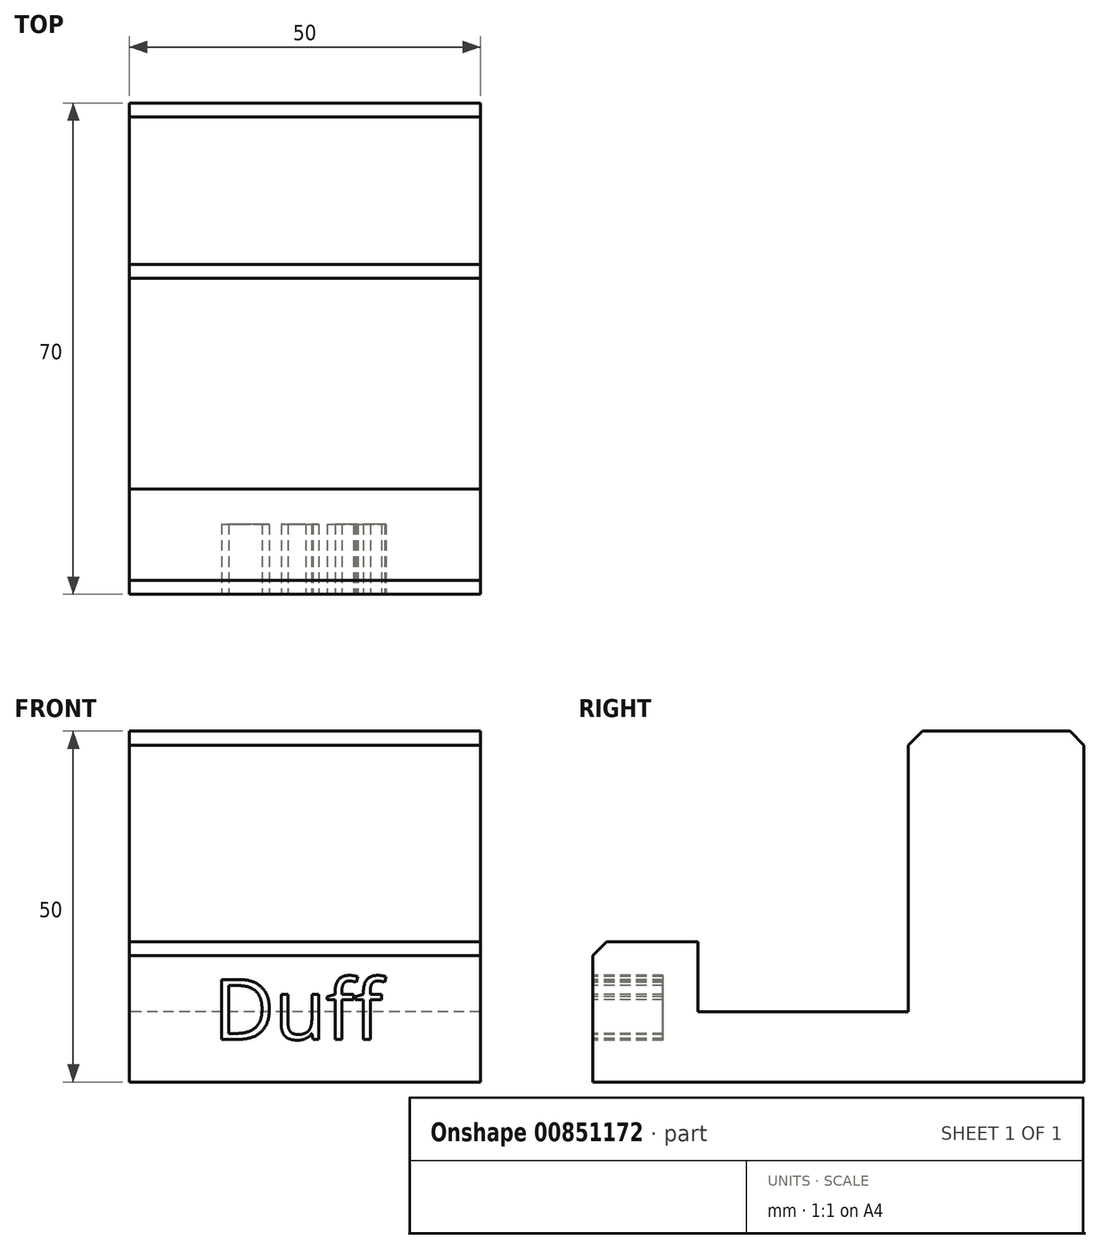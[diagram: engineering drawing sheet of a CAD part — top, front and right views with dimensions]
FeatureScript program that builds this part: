
annotation { "Feature Type Name" : "Feature", "Feature Type Description" : "" }
export const myFeature = defineFeature(function(context is Context, id is Id, definition is map)
    precondition{}
    {
        {
            var Q0;
            Q0=qCreatedBy(makeId("Right.planeOp"),FACE);
            var sketch = newSketch(context, id + "F0", { "sketchPlane" : qUnion([Q0])});
            skLineSegment(sketch, "E0", {"start": v(-40.46, 20) * mm, "end": v(-40.46, 0) * mm});
            skLineSegment(sketch, "E1", {"start": v(-40.46, 20) * mm, "end": v(-25.46, 20) * mm});
            skLineSegment(sketch, "E2", {"start": v(-40.46, 0) * mm, "end": v(29.54, 0) * mm});
            skLineSegment(sketch, "E3", {"start": v(29.54, 0) * mm, "end": v(29.54, 50) * mm});
            skLineSegment(sketch, "E4", {"start": v(29.54, 50) * mm, "end": v(4.54, 50) * mm});
            skLineSegment(sketch, "E5", {"start": v(4.54, 50) * mm, "end": v(4.54, 10) * mm});
            skLineSegment(sketch, "E6", {"start": v(4.54, 10) * mm, "end": v(-25.46, 10) * mm});
            skLineSegment(sketch, "E7", {"start": v(-25.46, 10) * mm, "end": v(-25.46, 20) * mm});
            skSolve(sketch);
        }
        {
            var Q0;
            Q0=makeQuery(id+"F0.imprint","IMPRINT",FACE,{"disambiguationData":[TD([[makeQuery(id+"F0.imprint","IMPRINT",EDGE,{"derivedFrom":sQuery(id+"F0.wireOp",EDGE,"E0")}),1.0]])]});
            extrude(context, id + "F1", {"entities" : qUnion([Q0]), "depth" : 50 * mm, "offsetDistance" : 25 * mm, "symmetric" : true});
        }
        {
            var Q0;
            Q0=makeQuery(id+"F1.opExtrude","SWEPT_FACE",FACE,{"disambiguationData":[OSD([sQuery(id+"F0.wireOp",EDGE,"E0")])]});
            var sketch = newSketch(context, id + "F2", { "sketchPlane" : qUnion([Q0])});
            skText(sketch, "E8", { "text": "Duff", "fontName": "OpenSans-Regular.ttf"});
            const initialGuessF2  = {"E8": [-0.01303, 0.00607, 1, 0, 0.00859]};
            skSetInitialGuess(sketch, initialGuessF2);
            skSolve(sketch);
        }
        {
            var Q0;
            Q0 = qSketchRegion(id + "F2", true);
            extrude(context, id + "F3", {"entities" : qUnion([Q0]), "operationType" : NewBodyOperationType.REMOVE, "oppositeDirection" : true, "depth" : 10 * mm, "offsetDistance" : 25 * mm});
        }
        {
            var Q0;
            Q0=makeQuery(id+"F1.opExtrude","SWEPT_EDGE",EDGE,{"disambiguationData":[OSD([sQuery(id+"F0.wireOp",EDGE,"E0"),sQuery(id+"F0.wireOp",EDGE,"E1")])]});
            var Q1;
            Q1=makeQuery(id+"F1.opExtrude","SWEPT_EDGE",EDGE,{"disambiguationData":[OSD([sQuery(id+"F0.wireOp",EDGE,"E3"),sQuery(id+"F0.wireOp",EDGE,"E4")])]});
            var Q2;
            Q2=makeQuery(id+"F1.opExtrude","SWEPT_EDGE",EDGE,{"disambiguationData":[OSD([sQuery(id+"F0.wireOp",EDGE,"E4"),sQuery(id+"F0.wireOp",EDGE,"E5")])]});
            chamfer(context, id + "F4", {"entities" : qUnion([Q0, Q1, Q2]), "width" : 2 * mm, "tangentPropagation" : true});
        }
    });
